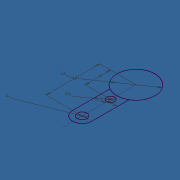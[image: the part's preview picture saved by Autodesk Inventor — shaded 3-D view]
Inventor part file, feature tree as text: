
AUTODESK INVENTOR PART (.ipt)
format: ipt  version: unknown  size: 229,888 bytes
history: native  units: mm
features: extrude x2, sketch x2, pattern_circular x1, chamfer x1
ambient origin geometry x8: Origin, YZ Plane, XZ Plane, XY Plane, X Axis, Y Axis, Z Axis, Center Point
bodies: Solid1 (feature_tree)
feature tree (6):
  extrude  "Extrusion1"  Depth=12.0mm
  extrude  "Extrusion2"  Depth=3.0mm
  pattern_circular  "Circular Pattern1"  [2 undecoded]
  chamfer  "Chamfer1"  Distance=9.0mm
  sketch  "Sketch2"  dims[d12=5.0mm d13=12.0mm]
  sketch  "Sketch3"  dims[d14=2.5mm d15=0.0mm d16=3.0mm d17=2.5mm d18=9.0mm d19=17.0mm d20=3.0mm d21=3.0mm d22=2.5mm d23=0.0mm d24=40.0mm d25=360.0deg d27=0.6mm d28=2.0mm d29=45.0deg]
note: 2 required parameter values undecoded (feature->parameter linkage not recoverable at this tier; creation-order binding heuristic only, values carry confidence <= 0.55)
